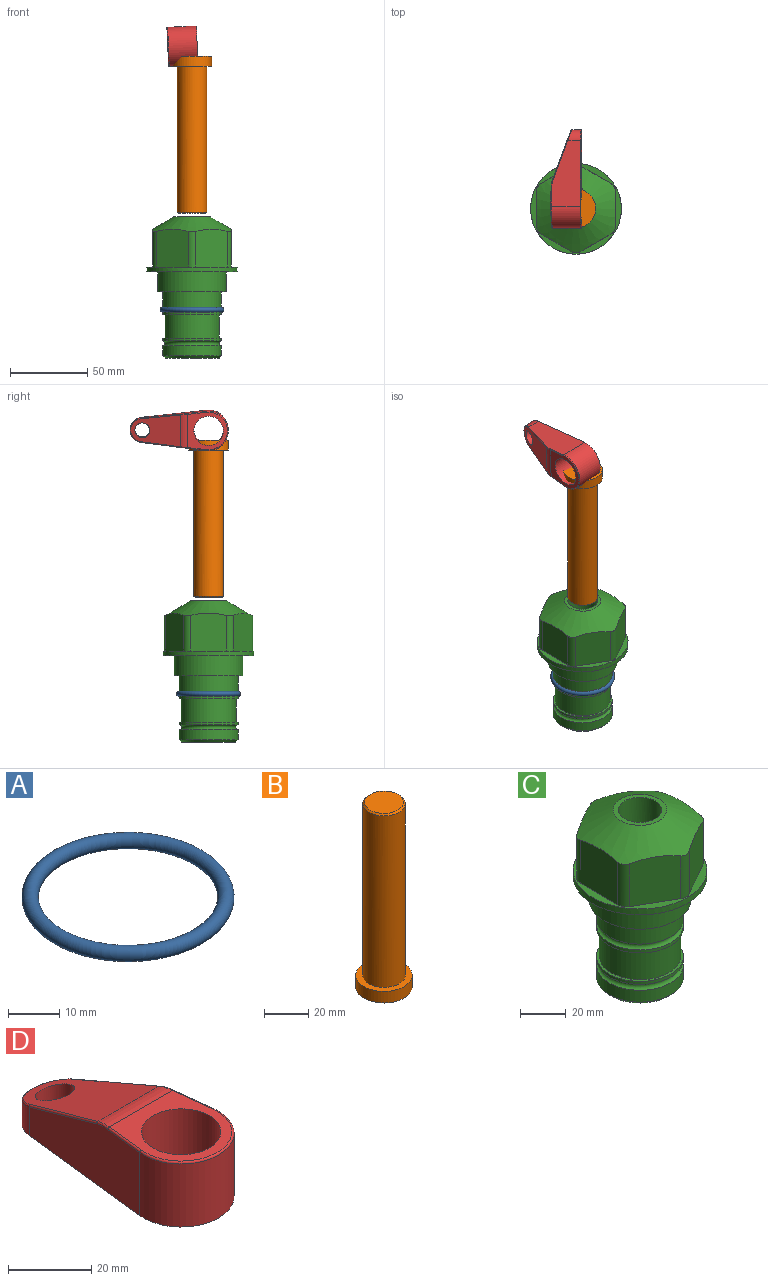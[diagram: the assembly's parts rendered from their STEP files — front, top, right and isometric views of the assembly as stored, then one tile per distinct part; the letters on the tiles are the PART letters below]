
ASSEMBLY  parts=4 mates=1
PART A: 1 faces, bbox 44.7x44.7x3.2 mm
  f0: torus R=19.05mm, axis (0,0,1), area 1193.9mm2
PART B: 6 faces, bbox 25.4x25.4x101.6 mm
  f0: plane 17.46x17.46mm, normal (0,0,1), area 239.5mm2, adj f5
  f1: plane 25.4x25.4mm, normal (0,0,-1), area 506.7mm2, adj f2
  f2: cylinder r=12.7mm len=25.4mm, axis (0,0,1), area 506.7mm2, adj f1,f3
  f3: plane 25.4x25.4mm, normal (0,0,1), area 221.7mm2, adj f2,f4
  f4: cylinder r=9.53mm len=94.46mm, axis (0,0,1), area 5653mm2, adj f3,f5
  f5: cone r=8.73mm half-angle=45deg, axis (0,0,-1), area 64.4mm2, adj f0,f4
PART C: 36 faces, bbox 58.7x58.7x91.2 mm
  f0: cylinder r=17.78mm len=35.56mm, axis (0,0,1), area 1670.8mm2, adj f23,f24,f31
  f1: cylinder r=19.05mm len=38.1mm, axis (0,0,1), area 1191.9mm2, adj f26,f27,f30
  f2: plane 58.66x58.66mm, normal (0,0,-1), area 1150.6mm2, adj f3,f28
  f3: cylinder r=29.33mm len=58.66mm, axis (0,0,-1), area 585.1mm2, adj f2,f4
  f4: plane 58.66x58.66mm, normal (0,0,1), area 475.9mm2, adj f3,f5,f6,f7,f8,f9,f10,f11
  f5: plane 24.5x20.32mm, normal (-0.5,0.87,0), area 562.8mm2, adj f4,f15,f16,f17
  f6: plane 24.5x20.32mm, normal (0.5,0.87,0), area 562.8mm2, adj f4,f14,f15,f17
  f7: plane 24.5x23.48mm, normal (1,0,0), area 562.8mm2, adj f4,f13,f14,f17
  f8: plane 24.5x20.32mm, normal (0.5,-0.87,0), area 562.8mm2, adj f4,f12,f13,f17
  f9: plane 24.5x20.32mm, normal (-0.5,-0.87,0), area 562.8mm2, adj f4,f11,f12,f17
  f10: plane 24.5x23.48mm, normal (-1,0,0), area 562.8mm2, adj f4,f11,f16,f17
  f11: cylinder r=5.08mm len=23.01mm, axis (0,0,-1), area 121.2mm2, adj f4,f9,f10,f17
  f12: cylinder r=5.08mm len=23.01mm, axis (0,0,-1), area 121.2mm2, adj f4,f8,f9,f17
  f13: cylinder r=5.08mm len=23.01mm, axis (0,0,-1), area 121.2mm2, adj f4,f7,f8,f17
  f14: cylinder r=5.08mm len=23.01mm, axis (0,0,-1), area 121.2mm2, adj f4,f6,f7,f17
  f15: cylinder r=5.08mm len=23.01mm, axis (0,0,-1), area 121.2mm2, adj f4,f5,f6,f17
  f16: cylinder r=5.08mm len=23.01mm, axis (0,0,-1), area 121.2mm2, adj f4,f5,f10,f17
  f17: cone r=11.73mm half-angle=60deg, axis (0,0,-1), area 2071.8mm2, adj f5,f6,f7,f8,f9,f10,f11,f12
  f18: plane 23.46x23.46mm, normal (0,0,1), area 147.4mm2, adj f17,f35
  f19: plane 34.93x34.93mm, normal (0,0,-1), area 958mm2, adj f29
  f20: cylinder r=19.05mm len=38.1mm, axis (0,0,1), area 760.1mm2, adj f21,f29
  f21: torus R=19.05mm, axis (0,0,1), area 565.3mm2, adj f20,f22
  f22: cylinder r=19.05mm len=38.1mm, axis (0,0,1), area 190mm2, adj f21,f23
  f23: plane 38.1x38.1mm, normal (0,0,1), area 146.9mm2, adj f0,f22
  f24: plane 38.1x38.1mm, normal (0,0,-1), area 146.9mm2, adj f0,f25
  f25: cylinder r=19.05mm len=38.1mm, axis (0,0,1), area 190mm2, adj f24,f26
  f26: torus R=19.05mm, axis (0,0,1), area 565.3mm2, adj f1,f25
  f27: plane 44.45x44.45mm, normal (0,0,-1), area 411.7mm2, adj f1,f28
  f28: cylinder r=22.23mm len=44.45mm, axis (0,0,1), area 1773.5mm2, adj f2,f27
  f29: cone r=19.05mm half-angle=45deg, axis (0,0,1), area 257.5mm2, adj f19,f20
  f30: cylinder r=3.17mm len=6.75mm, axis (-1,0,0), area 128mm2, adj f1,f33
  f31: cylinder r=3.17mm len=6.35mm, axis (-1,0,0), area 102.5mm2, adj f0,f33
  f32: plane 25.4x25.4mm, normal (0,0,1), area 506.7mm2, adj f33
  f33: cylinder r=12.7mm len=66.42mm, axis (0,0,-1), area 5236.2mm2, adj f30,f31,f32,f34
  f34: cone r=9.53mm half-angle=30deg, axis (0,0,-1), area 443.4mm2, adj f33,f35
  f35: cylinder r=9.53mm len=19.05mm, axis (0,0,-1), area 849mm2, adj f18,f34
PART D: 44 faces, bbox 27.5x64.5x19.1 mm
  f0: plane 2.3x0.95mm, normal (0,0,-1), area 1mm2, adj f25,f30,f34
  f1: plane 63.5x25.4mm, normal (0,0,-1), area 561.7mm2, adj f2,f3,f4,f5,f6,f7,f19,f20
  f2: cylinder r=12.7mm len=25.4mm, axis (0,0,-1), area 792.2mm2, adj f1,f3,f5,f13
  f3: plane 42.33x18.54mm, normal (0.99,0.11,0), area 647mm2, adj f1,f2,f4,f11,f12,f14
  f4: cylinder r=7.94mm len=15.78mm, axis (0,0,-1), area 158.6mm2, adj f1,f3,f5,f16
  f5: plane 42.33x18.54mm, normal (-0.99,0.11,0), area 647mm2, adj f1,f2,f4,f15,f17,f18
  f6: cylinder r=9.53mm len=19.05mm, axis (0,0,-1), area 1140.1mm2, adj f1,f8
  f7: cylinder r=4.76mm len=10.98mm, axis (0,0,-1), area 276.1mm2, adj f1,f9
  f8: plane 25.83x24.38mm, normal (0,0,1), area 262.2mm2, adj f6,f10,f11,f13,f15
  f9: plane 32.49x20.55mm, normal (0,0.34,0.94), area 489.9mm2, adj f7,f10,f14,f16,f18
  f10: cylinder r=12.7mm len=21.49mm, axis (-1,0,0), area 93.2mm2, adj f8,f9,f12,f17
  f11: cylinder r=0.51mm len=12.34mm, axis (0.11,-0.99,0), area 9.9mm2, adj f3,f8,f12,f13
  f12: bspline ~7.62x1.64mm, area 3.5mm2, adj f3,f10,f11,f14
  f13: torus R=12.19mm, axis (0,0,1), area 33.6mm2, adj f2,f8,f11,f15
  f14: cylinder r=0.51mm len=26.01mm, axis (0.1,-0.93,0.34), area 21.6mm2, adj f3,f9,f12,f16
  f15: cylinder r=0.51mm len=12.34mm, axis (0.11,0.99,0), area 9.9mm2, adj f5,f8,f13,f17
  f16: bspline ~15.78x7.05mm, area 15.7mm2, adj f4,f9,f14,f18
  f17: bspline ~7.62x1.64mm, area 3.5mm2, adj f5,f10,f15,f18
  f18: cylinder r=0.51mm len=26.01mm, axis (0.1,0.93,-0.34), area 21.6mm2, adj f5,f9,f16,f17
  f19: plane 21.6x14.29mm, normal (-0.99,-0.11,0), area 242.6mm2, adj f1,f26,f28,f34,f36,f38
  f20: plane 21.6x14.29mm, normal (0.99,-0.11,0), area 242.6mm2, adj f1,f27,f29,f37,f39,f41
  f21: cylinder r=12.7mm len=14.29mm, axis (0,0,-1), area 173.2mm2, adj f1,f26,f27,f30,f31,f33
  f22: cylinder r=7.94mm len=7.63mm, axis (0,0,-1), area 53.8mm2, adj f1,f28,f29,f42
  f23: plane 2.3x0.95mm, normal (0,0,-1), area 1mm2, adj f25,f33,f37
  f24: plane 17.94x12.32mm, normal (0,-0.34,-0.94), area 191.2mm2, adj f25,f38,f41,f42
  f25: cylinder r=9.53mm len=12.93mm, axis (-1,0,0), area 37.5mm2, adj f0,f23,f24,f31,f36,f39
  f26: cylinder r=1.59mm len=14.29mm, axis (0,0,-1), area 49mm2, adj f1,f19,f21,f32
  f27: cylinder r=1.59mm len=14.29mm, axis (0,0,-1), area 49mm2, adj f1,f20,f21,f35
  f28: cylinder r=1.59mm len=7.28mm, axis (0,0,-1), area 22.1mm2, adj f1,f19,f22,f40
  f29: cylinder r=1.59mm len=7.28mm, axis (0,0,-1), area 22.1mm2, adj f1,f20,f22,f43
  f30: torus R=14.29mm, axis (0,0,1), area 5.8mm2, adj f0,f21,f31,f32
  f31: bspline ~11.06x2.73mm, area 20.8mm2, adj f21,f25,f30,f33
  f32: sphere r=1.59mm, area 5.4mm2, adj f26,f30,f34
  f33: torus R=14.29mm, axis (0,0,1), area 5.8mm2, adj f21,f23,f31,f35
  f34: cylinder r=1.59mm len=1.68mm, axis (-0.11,0.99,0), area 2.4mm2, adj f0,f19,f32,f36
  f35: sphere r=1.59mm, area 5.4mm2, adj f27,f33,f37
  f36: bspline ~5.82x2.33mm, area 7.7mm2, adj f19,f25,f34,f38
  f37: cylinder r=1.59mm len=1.68mm, axis (0.11,0.99,0), area 2.4mm2, adj f20,f23,f35,f39
  f38: cylinder r=1.59mm len=18.33mm, axis (0.1,-0.93,0.34), area 46.7mm2, adj f19,f24,f36,f40
  f39: bspline ~5.82x2.33mm, area 7.7mm2, adj f20,f25,f37,f41
  f40: sphere r=1.59mm, area 3.6mm2, adj f28,f38,f42
  f41: cylinder r=1.59mm len=18.33mm, axis (0.1,0.93,-0.34), area 46.7mm2, adj f20,f24,f39,f43
  f42: bspline ~8.31x1.84mm, area 15.3mm2, adj f22,f24,f40,f43
  f43: sphere r=1.59mm, area 3.6mm2, adj f29,f41,f42
PLACE A t=(67.21,42.11,-4.06)mm
PLACE B rot(axis=(1,0,0),180deg) t=(67.21,42.11,107.43)mm
PLACE C t=(67.21,42.11,-4.06)mm
PLACE D rot(axis=(0,-1,0),92.6deg) t=(70.59,42.11,142.23)mm
MATE slider C.f0 <-> B.f2  axis (0,0,1) through (67.21,42.11,31.5)mm
